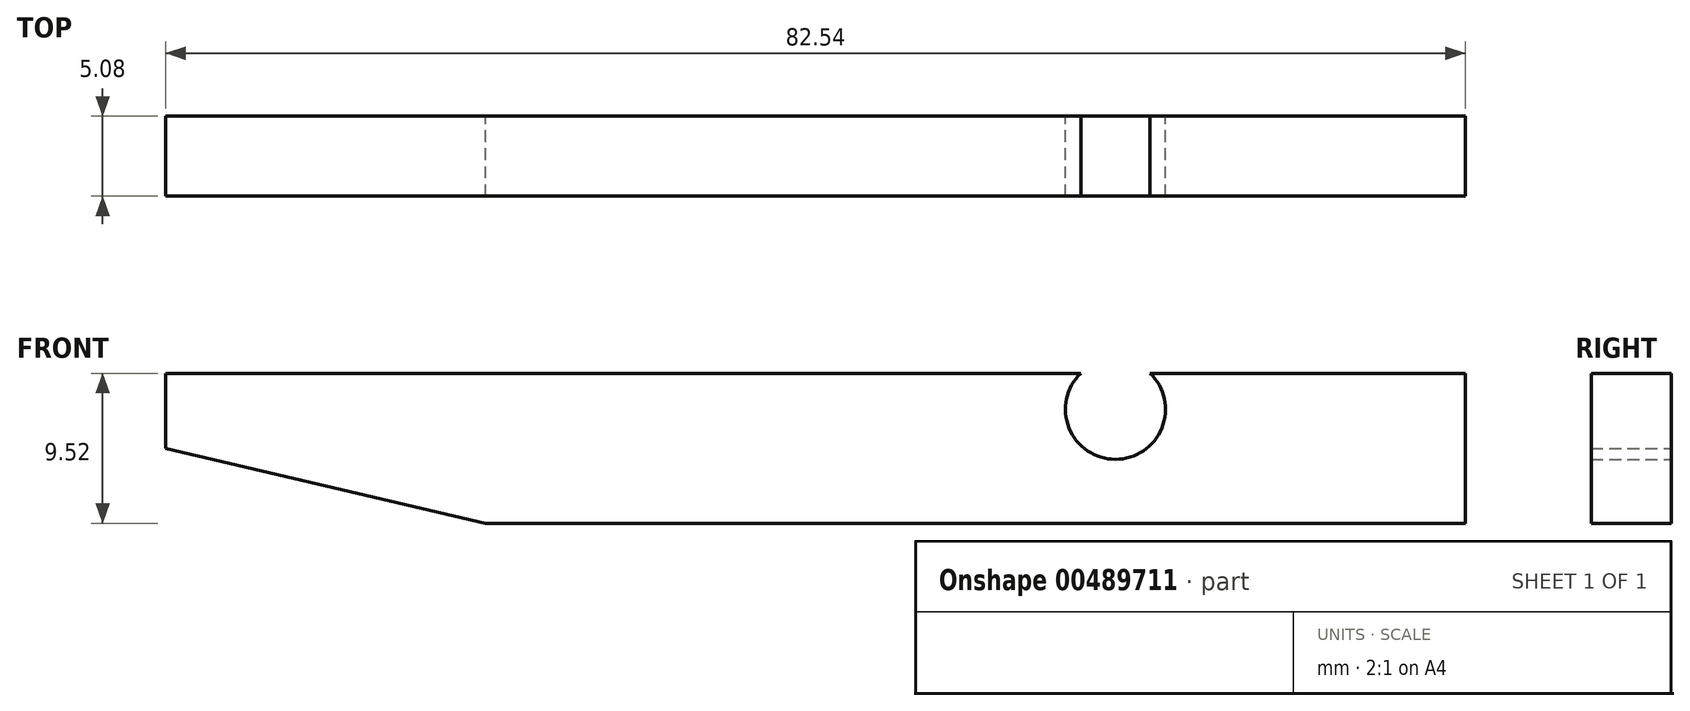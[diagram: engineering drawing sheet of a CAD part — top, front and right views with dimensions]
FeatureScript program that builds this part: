
annotation { "Feature Type Name" : "Feature", "Feature Type Description" : "" }
export const myFeature = defineFeature(function(context is Context, id is Id, definition is map)
    precondition{}
    {
        {
            var Q0;
            Q0=qCreatedBy(makeId("Front.planeOp"),FACE);
            var sketch = newSketch(context, id + "F0", { "sketchPlane" : qUnion([Q0])});
            skLineSegment(sketch, "E0.bottom", {"start": v(41.28, 4.76) * mm, "end": v(24.13, 4.76) * mm});
            skLineSegment(sketch, "E0.top", {"start": v(41.28, -4.76) * mm, "end": v(-20.96, -4.76) * mm});
            skLineSegment(sketch, "E0.left", {"start": v(41.28, 4.76) * mm, "end": v(41.28, -4.76) * mm});
            skLineSegment(sketch, "E0.right", {"start": v(-41.28, 4.76) * mm, "end": v(-41.28, 0) * mm});
            skPoint(sketch, "E0.middle", {"position": v(0, 0) * mm});
            skPoint(sketch, "E1.orphan", {"position": v(19.05, 4.76) * mm});
            skLineSegment(sketch, "E2.trimOffspring", {"start": v(13.97, 4.76) * mm, "end": v(-41.28, 4.76) * mm});
            skLineSegment(sketch, "E3", {"start": v(-41.28, 0) * mm, "end": v(-20.95, -4.76) * mm});
            skPoint(sketch, "E4.orphan", {"position": v(-41.28, -4.76) * mm});
            skPoint(sketch, "E5.end.orphan", {"position": v(19.05, -4.76) * mm});
            skLineSegment(sketch, "E6", {"start": v(13.97, 4.76) * mm, "end": v(16.85, 4.76) * mm});
            skLineSegment(sketch, "E7", {"start": v(19.05, 4.76) * mm, "end": v(19.05, 2.48) * mm, "construction": true});
            skArc(sketch, "E8", {"start": v(16.85, 4.76) * mm, "mid": v(19.05, -0.7) * mm, "end": v(21.25, 4.76) * mm});
            skLineSegment(sketch, "E9.trimOffspring", {"start": v(21.25, 4.76) * mm, "end": v(24.13, 4.76) * mm});
            skSolve(sketch);
        }
        {
            var Q0;
            Q0=makeQuery(id+"F0.imprint","IMPRINT",FACE,{"disambiguationData":[TD([[makeQuery(id+"F0.imprint","IMPRINT",EDGE,{"derivedFrom":sQuery(id+"F0.wireOp",EDGE,"E0.bottom")}),1.0]])]});
            extrude(context, id + "F1", {"entities" : qUnion([Q0]), "depth" : 5.08 * mm});
        }
    });
